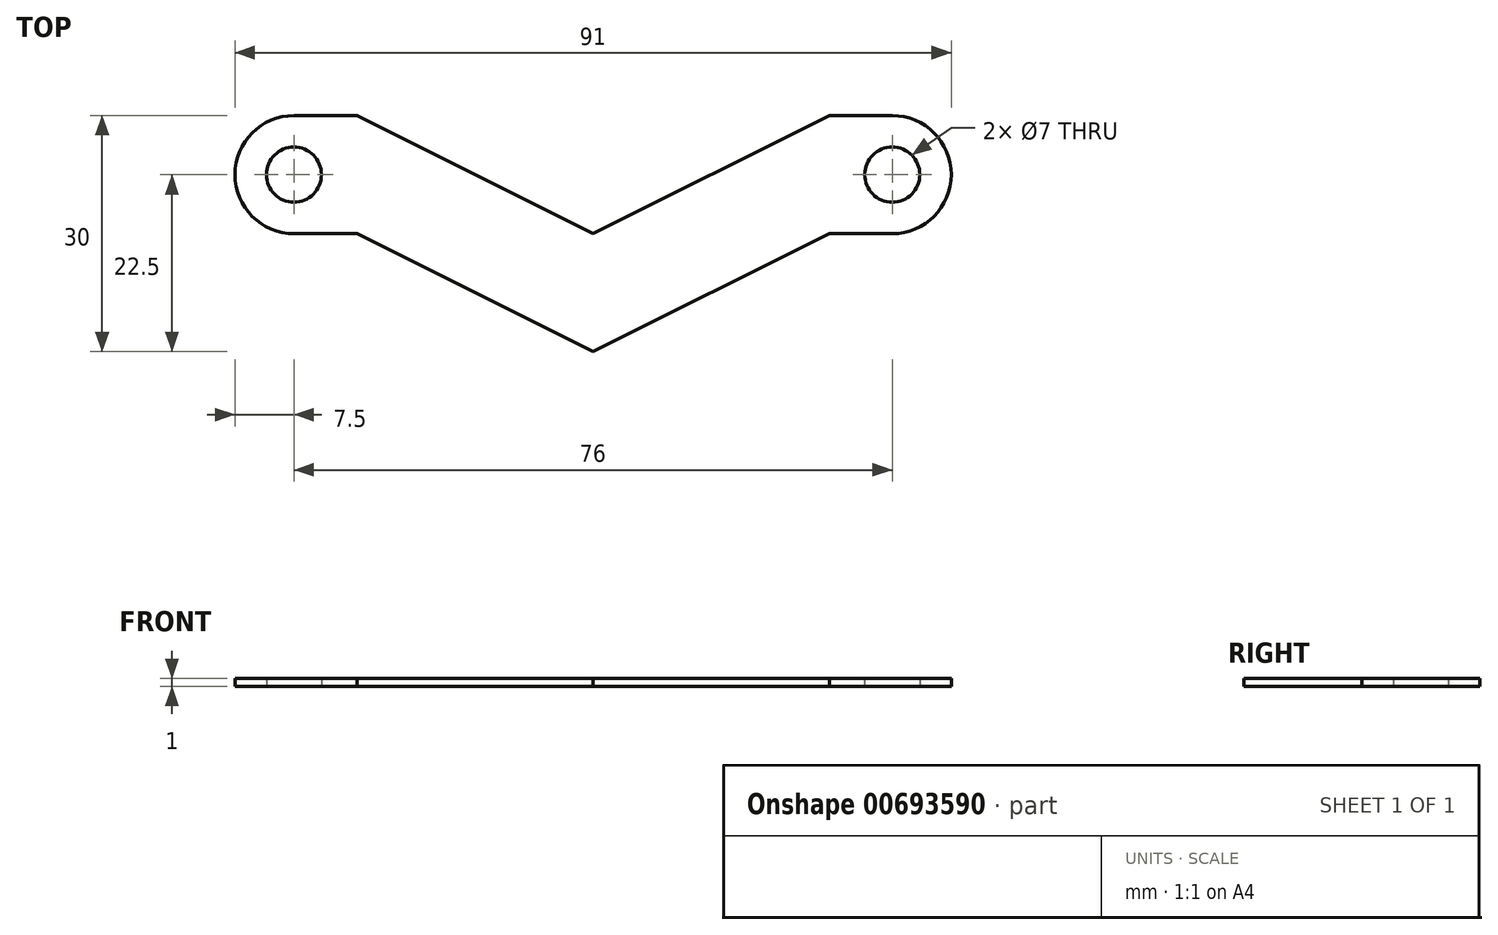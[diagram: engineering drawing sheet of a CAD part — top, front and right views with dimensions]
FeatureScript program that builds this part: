
annotation { "Feature Type Name" : "Feature", "Feature Type Description" : "" }
export const myFeature = defineFeature(function(context is Context, id is Id, definition is map)
    precondition{}
    {
        {
            var Q0;
            Q0=qCreatedBy(makeId("Top.planeOp"),FACE);
            var sketch = newSketch(context, id + "F0", { "sketchPlane" : qUnion([Q0])});
            skLineSegment(sketch, "E0", {"start": v(0, 0) * mm, "end": v(-30, 0) * mm, "construction": true});
            skLineSegment(sketch, "E1", {"start": v(0, -15) * mm, "end": v(-30, -15) * mm, "construction": true});
            skLineSegment(sketch, "E2", {"start": v(-30, 0) * mm, "end": v(-38, 0) * mm});
            skLineSegment(sketch, "E3", {"start": v(-38, 0) * mm, "end": v(-38, -15) * mm, "construction": true});
            skLineSegment(sketch, "E4", {"start": v(-38, -15) * mm, "end": v(-30, -15) * mm});
            skLineSegment(sketch, "E5", {"start": v(-30, 0) * mm, "end": v(-30, -15) * mm});
            skArc(sketch, "E6", {"start": v(-38, 0) * mm, "mid": v(-45.5, -7.5) * mm, "end": v(-38, -15) * mm});
            skLineSegment(sketch, "E7", {"start": v(0, 17.93) * mm, "end": v(0, -59.06) * mm, "construction": true});
            skLineSegment(sketch, "E8.MirrorCS", {"start": v(38, 0) * mm, "end": v(38, -15) * mm, "construction": true});
            skLineSegment(sketch, "E9.MirrorCS", {"start": v(38, -15) * mm, "end": v(30, -15) * mm});
            skLineSegment(sketch, "E10.MirrorCS", {"start": v(30, 0) * mm, "end": v(30, -15) * mm});
            skLineSegment(sketch, "E11.MirrorCS", {"start": v(30, 0) * mm, "end": v(38, 0) * mm});
            skLineSegment(sketch, "E12.MirrorCS", {"start": v(0, -15) * mm, "end": v(30, -15) * mm, "construction": true});
            skLineSegment(sketch, "E13.MirrorCS", {"start": v(0, 0) * mm, "end": v(30, 0) * mm, "construction": true});
            skArc(sketch, "E14.MirrorCS", {"start": v(38, 0) * mm, "mid": v(45.5, -7.5) * mm, "end": v(38, -15) * mm});
            skLineSegment(sketch, "E15", {"start": v(-30, 0) * mm, "end": v(0, -15) * mm});
            skLineSegment(sketch, "E16", {"start": v(-30, -15) * mm, "end": v(0, -30) * mm});
            skLineSegment(sketch, "E17.MirrorCS", {"start": v(30, 0) * mm, "end": v(0, -15) * mm});
            skLineSegment(sketch, "E18.MirrorCS", {"start": v(30, -15) * mm, "end": v(0, -30) * mm});
            skCircle(sketch, "E19", {"center": v(-38, -7.5) * mm, "radius": 3.5 * mm});
            skCircle(sketch, "E20.MirrorC", {"center": v(38, -7.5) * mm, "radius": 3.5 * mm});
            skLineSegment(sketch, "E21", {"start": v(0, -15) * mm, "end": v(0, -30) * mm});
            skSolve(sketch);
        }
        {
            var Q0;
            Q0=makeQuery(id+"F0.imprint","IMPRINT",FACE,{"disambiguationData":[TD([[makeQuery(id+"F0.imprint","IMPRINT",EDGE,{"derivedFrom":sQuery(id+"F0.wireOp",EDGE,"E5")}),1.0]])]});
            var Q1;
            Q1=makeQuery(id+"F0.imprint","IMPRINT",FACE,{"disambiguationData":[TD([[makeQuery(id+"F0.imprint","IMPRINT",EDGE,{"derivedFrom":sQuery(id+"F0.wireOp",EDGE,"E10.MirrorCS")}),-1.0]])]});
            var Q2;
            Q2=makeQuery(id+"F0.imprint","IMPRINT",FACE,{"disambiguationData":[TD([[makeQuery(id+"F0.imprint","IMPRINT",EDGE,{"derivedFrom":sQuery(id+"F0.wireOp",EDGE,"E9.MirrorCS")}),-1.0]])]});
            var Q3;
            Q3=makeQuery(id+"F0.imprint","IMPRINT",FACE,{"disambiguationData":[TD([[makeQuery(id+"F0.imprint","IMPRINT",EDGE,{"derivedFrom":sQuery(id+"F0.wireOp",EDGE,"E2")}),1.0]])]});
            extrude(context, id + "F1", {"entities" : qUnion([Q0, Q1, Q2, Q3]), "depth" : 1 * mm, "offsetDistance" : 25 * mm});
        }
    });
